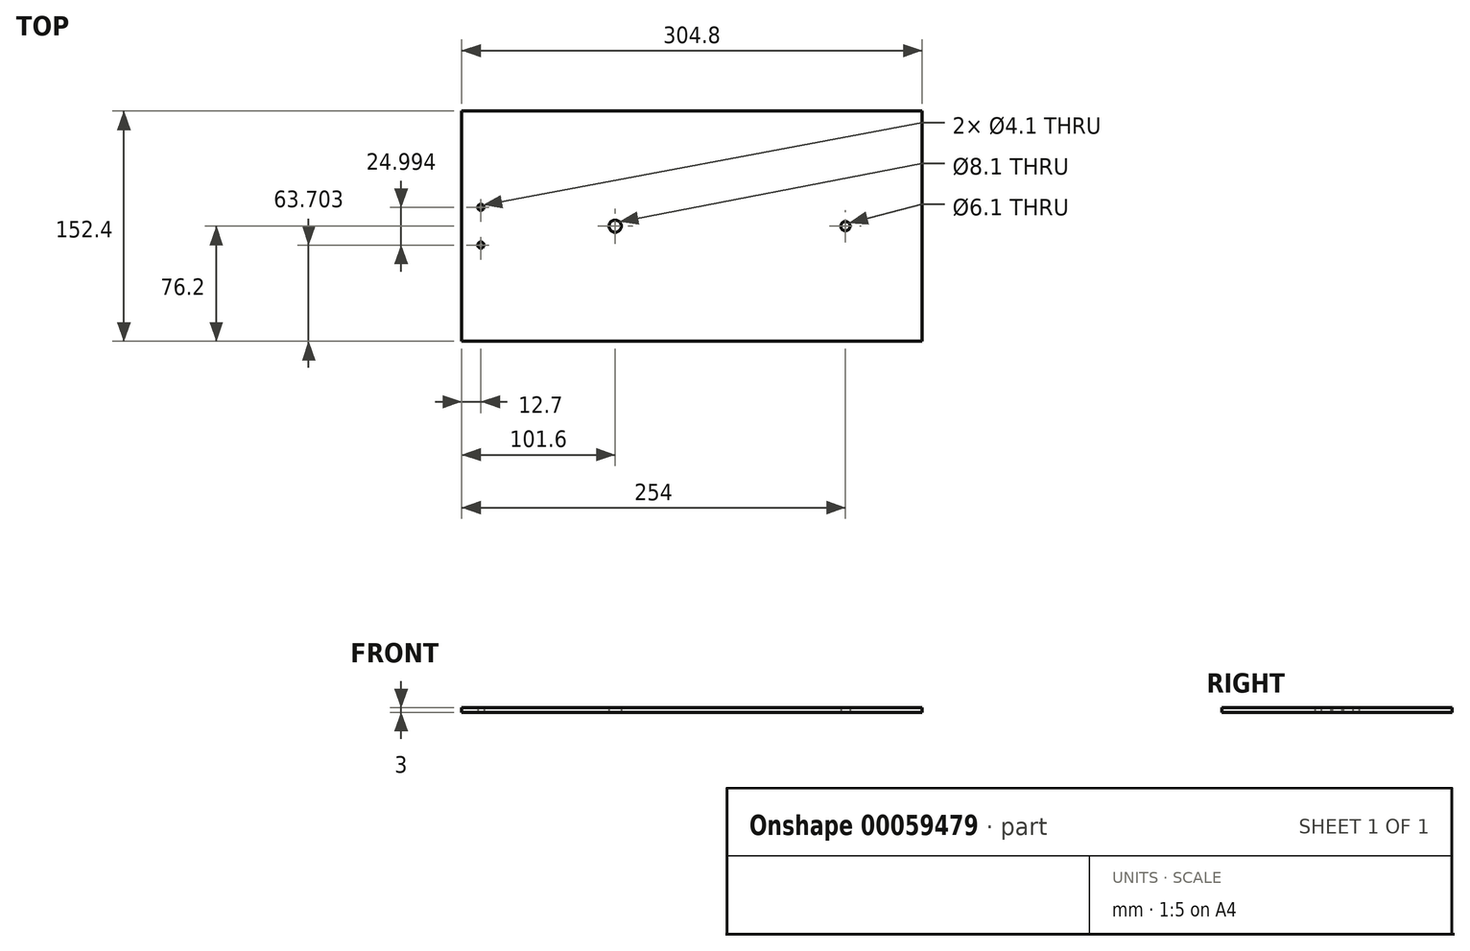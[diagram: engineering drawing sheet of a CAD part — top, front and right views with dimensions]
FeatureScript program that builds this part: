
annotation { "Feature Type Name" : "Feature", "Feature Type Description" : "" }
export const myFeature = defineFeature(function(context is Context, id is Id, definition is map)
    precondition{}
    {
        {
            var Q0;
            Q0=qCreatedBy(makeId("Top.planeOp"),FACE);
            var sketch = newSketch(context, id + "F0", { "sketchPlane" : qUnion([Q0])});
            skLineSegment(sketch, "E0.rect.bottom", {"start": v(-152.4, -76.2) * mm, "end": v(152.4, -76.2) * mm});
            skLineSegment(sketch, "E0.rect.top", {"start": v(-152.4, 76.2) * mm, "end": v(152.4, 76.2) * mm});
            skLineSegment(sketch, "E0.rect.left", {"start": v(-152.4, -76.2) * mm, "end": v(-152.4, 76.2) * mm});
            skLineSegment(sketch, "E0.rect.right", {"start": v(152.4, -76.2) * mm, "end": v(152.4, 76.2) * mm});
            skPoint(sketch, "E0.rect.middle", {"position": v(0, 0) * mm});
            skLineSegment(sketch, "E1", {"start": v(-152.4, 0) * mm, "end": v(152.4, 0) * mm, "construction": true});
            skCircle(sketch, "E2", {"center": v(101.6, 0) * mm, "radius": 3.05 * mm});
            skCircle(sketch, "E3", {"center": v(-50.8, 0) * mm, "radius": 4.05 * mm});
            skLineSegment(sketch, "E4", {"start": v(-139.7, -76.2) * mm, "end": v(-139.7, -12.5) * mm, "construction": true});
            skCircle(sketch, "E5", {"center": v(-139.7, -12.5) * mm, "radius": 2.05 * mm});
            skLineSegment(sketch, "E6", {"start": v(-139.7, -76.2) * mm, "end": v(-139.7, 12.5) * mm, "construction": true});
            skCircle(sketch, "E7", {"center": v(-139.7, 12.5) * mm, "radius": 2.05 * mm});
            skSolve(sketch);
        }
        {
            var Q0;
            Q0=makeQuery(id+"F0.imprint","IMPRINT",FACE,{"disambiguationData":[TD([[makeQuery(id+"F0.imprint","IMPRINT",EDGE,{"derivedFrom":sQuery(id+"F0.wireOp",EDGE,"E0.rect.bottom")}),1.0]])]});
            extrude(context, id + "F1", {"entities" : qUnion([Q0]), "depth" : 3 * mm});
        }
    });
